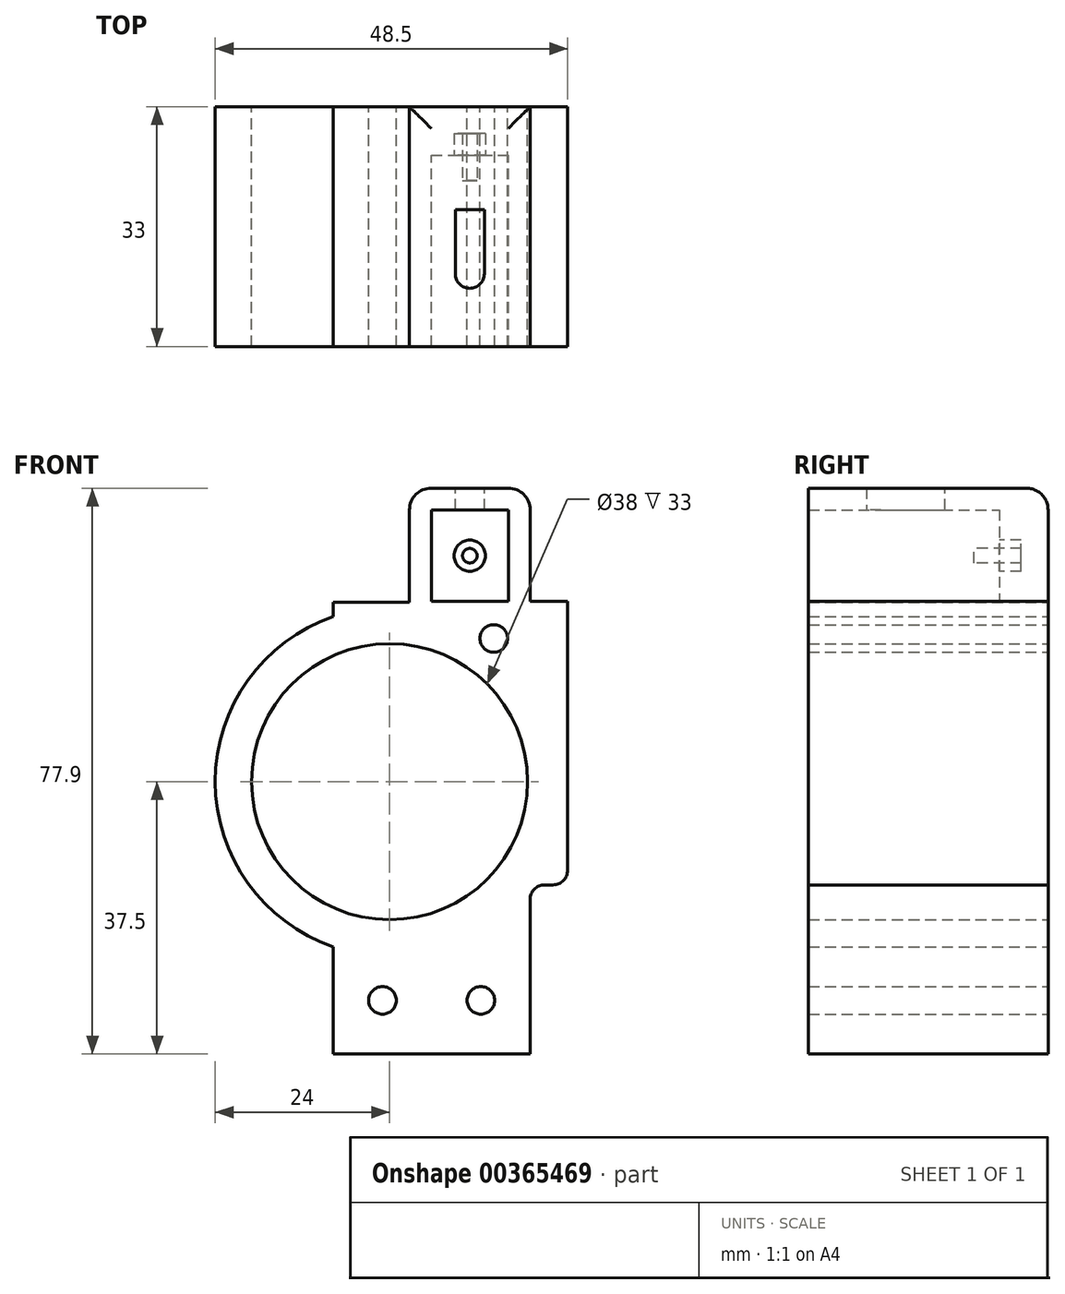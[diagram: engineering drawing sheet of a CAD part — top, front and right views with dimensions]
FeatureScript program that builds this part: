
annotation { "Feature Type Name" : "Feature", "Feature Type Description" : "" }
export const myFeature = defineFeature(function(context is Context, id is Id, definition is map)
    precondition{}
    {
        {
            var Q0;
            Q0=qCreatedBy(makeId("Front.planeOp"),FACE);
            var sketch = newSketch(context, id + "F0", { "sketchPlane" : qUnion([Q0])});
            skLineSegment(sketch, "E0", {"start": v(-117.96, -5.3) * mm, "end": v(-112.66, -5.3) * mm});
            skLineSegment(sketch, "E1", {"start": v(-112.66, -5.3) * mm, "end": v(-112.66, 7.3) * mm});
            skLineSegment(sketch, "E2", {"start": v(-112.66, 7.3) * mm, "end": v(-123.26, 7.3) * mm});
            skLineSegment(sketch, "E3", {"start": v(-123.26, 7.3) * mm, "end": v(-123.26, -5.3) * mm});
            skLineSegment(sketch, "E4", {"start": v(-123.26, -5.3) * mm, "end": v(-117.96, -5.3) * mm});
            skLineSegment(sketch, "E5.top", {"start": v(-109.66, 10.3) * mm, "end": v(-126.26, 10.3) * mm});
            skLineSegment(sketch, "E5.left", {"start": v(-109.66, 0) * mm, "end": v(-109.66, 10.3) * mm});
            skLineSegment(sketch, "E5.right", {"start": v(-126.26, 0) * mm, "end": v(-126.26, 10.3) * mm});
            skPoint(sketch, "E5.middle", {"position": v(-117.96, 1) * mm});
            skPoint(sketch, "E5.middle.positionSnap0", {"position": v(-123.26, 1) * mm});
            skPoint(sketch, "E5.middle.positionSnap1", {"position": v(-117.96, 7.3) * mm});
            skPoint(sketch, "E5.centerSnap0", {"position": v(-123.26, 1) * mm});
            skPoint(sketch, "E5.centerSnap1", {"position": v(-117.96, 7.3) * mm});
            skPoint(sketch, "E5.bottom.end.orphan", {"position": v(-126.26, -8.3) * mm});
            skPoint(sketch, "E6.orphan", {"position": v(-109.66, -8.3) * mm});
            skCircle(sketch, "E7", {"center": v(-129, -30.1) * mm, "radius": 19 * mm});
            skLineSegment(sketch, "E8", {"start": v(-126.26, 0) * mm, "end": v(-126.26, -5) * mm});
            skLineSegment(sketch, "E9", {"start": v(-109.66, 0) * mm, "end": v(-109.66, -5.3) * mm});
            skLineSegment(sketch, "E10", {"start": v(-109.66, -67.6) * mm, "end": v(-109.66, -44.31) * mm});
            skArc(sketch, "E11.trimOffspring", {"start": v(-136.75, -7.39) * mm, "mid": v(-153, -30.1) * mm, "end": v(-136.75, -52.81) * mm});
            skLineSegment(sketch, "E12", {"start": v(-126.26, -5) * mm, "end": v(-126.26, -5.4) * mm});
            skLineSegment(sketch, "E13", {"start": v(-126.26, -5.4) * mm, "end": v(-136.75, -5.4) * mm});
            skLineSegment(sketch, "E14", {"start": v(-136.75, -5.4) * mm, "end": v(-136.75, -7.39) * mm});
            skLineSegment(sketch, "E15", {"start": v(-109.66, -67.6) * mm, "end": v(-132.81, -67.6) * mm});
            skPoint(sketch, "E16.start.orphan", {"position": v(-109.66, -68) * mm});
            skLineSegment(sketch, "E17", {"start": v(-136.75, -52.81) * mm, "end": v(-136.75, -67.6) * mm});
            skLineSegment(sketch, "E18", {"start": v(-136.75, -67.6) * mm, "end": v(-132.81, -67.6) * mm});
            skLineSegment(sketch, "E19", {"start": v(-109.66, -15.89) * mm, "end": v(-114.66, -15.89) * mm});
            skCircle(sketch, "E20", {"center": v(-114.66, -10.39) * mm, "radius": 1.9 * mm});
            skLineSegment(sketch, "E21", {"start": v(-123.2, -60.2) * mm, "end": v(-123.2, -65.78) * mm});
            skPoint(sketch, "E22.orphan", {"position": v(-109.66, -60.2) * mm});
            skCircle(sketch, "E23", {"center": v(-129.98, -60.2) * mm, "radius": 1.9 * mm});
            skCircle(sketch, "E24.MirrorC", {"center": v(-116.43, -60.2) * mm, "radius": 1.9 * mm});
            skLineSegment(sketch, "E25", {"start": v(-109.66, -44.31) * mm, "end": v(-105, -44.31) * mm});
            skPoint(sketch, "E25.endSnap0", {"position": v(-105, -30.1) * mm});
            skLineSegment(sketch, "E26", {"start": v(-109.66, -5.3) * mm, "end": v(-105, -5.3) * mm});
            skLineSegment(sketch, "E27.bottom", {"start": v(-105, -5.3) * mm, "end": v(-104.5, -5.3) * mm});
            skLineSegment(sketch, "E27.top", {"start": v(-105, -44.31) * mm, "end": v(-104.5, -44.31) * mm});
            skLineSegment(sketch, "E27.right", {"start": v(-104.5, -5.3) * mm, "end": v(-104.5, -44.31) * mm});
            skSolve(sketch);
        }
        {
            var Q0;
            Q0 = qSketchRegion(id + "F0", true);
            extrude(context, id + "F1", {"entities" : qUnion([Q0]), "depth" : 33 * mm});
        }
        {
            var Q0;
            Q0=makeQuery(id+"F1.opExtrude","CAP_FACE",FACE,{"disambiguationData":[OSD([sQuery(id+"F0.wireOp",EDGE,"E0"),sQuery(id+"F0.wireOp",EDGE,"E1"),sQuery(id+"F0.wireOp",EDGE,"E2"),sQuery(id+"F0.wireOp",EDGE,"E3"),sQuery(id+"F0.wireOp",EDGE,"E4"),sQuery(id+"F0.wireOp",EDGE,"E5.top"),sQuery(id+"F0.wireOp",EDGE,"E5.left"),sQuery(id+"F0.wireOp",EDGE,"E5.right"),sQuery(id+"F0.wireOp",EDGE,"E7"),sQuery(id+"F0.wireOp",EDGE,"aaagPdJ2-hpna-5XmJ-qMSG-0a7ja9otKFb6"),sQuery(id+"F0.wireOp",EDGE,"E8"),sQuery(id+"F0.wireOp",EDGE,"E9"),sQuery(id+"F0.wireOp",EDGE,"E10"),sQuery(id+"F0.wireOp",EDGE,"E11.trimOffspring"),sQuery(id+"F0.wireOp",EDGE,"E12"),sQuery(id+"F0.wireOp",EDGE,"E13"),sQuery(id+"F0.wireOp",EDGE,"E14"),sQuery(id+"F0.wireOp",EDGE,"E15"),sQuery(id+"F0.wireOp",EDGE,"E17"),sQuery(id+"F0.wireOp",EDGE,"E18"),sQuery(id+"F0.wireOp",EDGE,"E20"),sQuery(id+"F0.wireOp",EDGE,"E23"),sQuery(id+"F0.wireOp",EDGE,"E24.MirrorC")])],"isStart":true});
            var sketch = newSketch(context, id + "F2", { "sketchPlane" : qUnion([Q0])});
            skLineSegment(sketch, "E28.bottom", {"start": v(123.26, 7.3) * mm, "end": v(112.66, 7.3) * mm});
            skLineSegment(sketch, "E28.top", {"start": v(123.26, -5.3) * mm, "end": v(112.66, -5.3) * mm});
            skLineSegment(sketch, "E28.left", {"start": v(123.26, 7.3) * mm, "end": v(123.26, -5.3) * mm});
            skLineSegment(sketch, "E28.right", {"start": v(112.66, 7.3) * mm, "end": v(112.66, -5.3) * mm});
            skSolve(sketch);
        }
        {
            var Q0;
            Q0 = qSketchRegion(id + "F2", true);
            extrude(context, id + "F3", {"entities" : qUnion([Q0]), "operationType" : NewBodyOperationType.ADD, "oppositeDirection" : true, "depth" : 6.7 * mm});
        }
        {
            var Q0;
            Q0=makeQuery(id+"F1.opExtrude","SWEPT_EDGE",EDGE,{"disambiguationData":[OSD([sQuery(id+"F0.wireOp",EDGE,"E5.top"),sQuery(id+"F0.wireOp",EDGE,"E5.left")])]});
            var Q1;
            Q1=makeQuery(id+"F1.opExtrude","SWEPT_EDGE",EDGE,{"disambiguationData":[OSD([sQuery(id+"F0.wireOp",EDGE,"E5.top"),sQuery(id+"F0.wireOp",EDGE,"E5.right")])]});
            var Q2;
            Q2=makeQuery(id+"F1.opExtrude","CAP_EDGE",EDGE,{"disambiguationData":[OSD([sQuery(id+"F0.wireOp",EDGE,"E5.top")])],"isStart":true});
            fillet(context, id + "F4", {"entities" : qUnion([Q0, Q1, Q2]), "radius" : 3 * mm, "tangentPropagation" : true, "allowEdgeOverflow" : false});
        }
        {
            var Q0;
            Q0=makeQuery(id+"F1.opExtrude","SWEPT_EDGE",EDGE,{"disambiguationData":[OSD([sQuery(id+"F0.wireOp",EDGE,"E27.top"),sQuery(id+"F0.wireOp",EDGE,"E27.right")])]});
            var Q1;
            Q1=makeQuery(id+"F1.opExtrude","SWEPT_EDGE",EDGE,{"disambiguationData":[OSD([sQuery(id+"F0.wireOp",EDGE,"E10"),sQuery(id+"F0.wireOp",EDGE,"E25")])]});
            fillet(context, id + "F5", {"entities" : qUnion([Q0, Q1]), "radius" : 2 * mm, "tangentPropagation" : true, "allowEdgeOverflow" : false});
        }
        {
            var Q0;
            Q0=makeQuery(id+"F1.opExtrude","SWEPT_FACE",FACE,{"disambiguationData":[OSD([sQuery(id+"F0.wireOp",EDGE,"E5.top")])]});
            var sketch = newSketch(context, id + "F6", { "sketchPlane" : qUnion([Q0])});
            skLineSegment(sketch, "E29", {"start": v(-117.96, -33) * mm, "end": v(-117.96, -25) * mm});
            skLineSegment(sketch, "E30", {"start": v(-117.96, -25) * mm, "end": v(-115.96, -25) * mm});
            skLineSegment(sketch, "E31", {"start": v(-115.96, -25) * mm, "end": v(-115.96, -14.2) * mm});
            skLineSegment(sketch, "E32", {"start": v(-115.96, -14.2) * mm, "end": v(-119.96, -14.2) * mm});
            skLineSegment(sketch, "E33", {"start": v(-119.96, -14.2) * mm, "end": v(-119.96, -25) * mm});
            skLineSegment(sketch, "E34", {"start": v(-119.96, -25) * mm, "end": v(-117.96, -25) * mm});
            skSolve(sketch);
        }
        {
            var Q0;
            Q0 = qSketchRegion(id + "F6", true);
            extrude(context, id + "F7", {"entities" : qUnion([Q0]), "operationType" : NewBodyOperationType.REMOVE, "oppositeDirection" : true, "depth" : 8.5 * mm});
        }
        {
            var Q0;
            Q0=makeQuery(id+"F7.boolean.opBoolean","COPY",EDGE,{"derivedFrom":makeQuery(id+"F7.opExtrude","SWEPT_EDGE",EDGE,{"disambiguationData":[OSD([sQuery(id+"F6.wireOp",EDGE,"E33"),sQuery(id+"F6.wireOp",EDGE,"E34")])]})});
            var Q1;
            Q1=makeQuery(id+"F7.boolean.opBoolean","COPY",EDGE,{"derivedFrom":makeQuery(id+"F7.opExtrude","SWEPT_EDGE",EDGE,{"disambiguationData":[OSD([sQuery(id+"F6.wireOp",EDGE,"E30"),sQuery(id+"F6.wireOp",EDGE,"E31")])]})});
            fillet(context, id + "F8", {"entities" : qUnion([Q0, Q1]), "radius" : 2 * mm, "tangentPropagation" : true, "allowEdgeOverflow" : false});
        }
        {
            var Q0;
            Q0=makeQuery(id+"F3.opExtrude","CAP_FACE",FACE,{"disambiguationData":[OSD([sQuery(id+"F2.wireOp",EDGE,"E28.bottom"),sQuery(id+"F2.wireOp",EDGE,"E28.top"),sQuery(id+"F2.wireOp",EDGE,"E28.left"),sQuery(id+"F2.wireOp",EDGE,"E28.right")])],"isStart":false});
            var sketch = newSketch(context, id + "F9", { "sketchPlane" : qUnion([Q0])});
            skCircle(sketch, "E35", {"center": v(-117.96, 1) * mm, "radius": 2.15 * mm});
            skPoint(sketch, "E35.centerSnap0", {"position": v(-117.96, -5.3) * mm});
            skPoint(sketch, "E35.centerSnap1", {"position": v(-123.26, 1) * mm});
            skCircle(sketch, "E36", {"center": v(-117.96, 1) * mm, "radius": 1 * mm});
            skSolve(sketch);
        }
        {
            var Q0;
            Q0 = qSketchRegion(id + "F9", true);
            extrude(context, id + "F10", {"entities" : qUnion([Q0]), "operationType" : NewBodyOperationType.REMOVE, "oppositeDirection" : true, "depth" : 3 * mm});
        }
        {
            var Q0;
            Q0=makeQuery(id+"F10.boolean.opBoolean","SPLIT",FACE,{"disambiguationData":[TD([makeQuery(id+"F10.opExtrude","SWEPT_FACE",FACE,{"disambiguationData":[OSD([sQuery(id+"F9.wireOp",EDGE,"E36")])]})])],"derivedFrom":makeQuery(id+"F3.opExtrude","CAP_FACE",FACE,{"disambiguationData":[OSD([sQuery(id+"F2.wireOp",EDGE,"E28.bottom"),sQuery(id+"F2.wireOp",EDGE,"E28.top"),sQuery(id+"F2.wireOp",EDGE,"E28.left"),sQuery(id+"F2.wireOp",EDGE,"E28.right")])],"isStart":false})});
            extrude(context, id + "F11", {"entities" : qUnion([Q0]), "operationType" : NewBodyOperationType.ADD, "depth" : 3.5 * mm});
        }
    });
